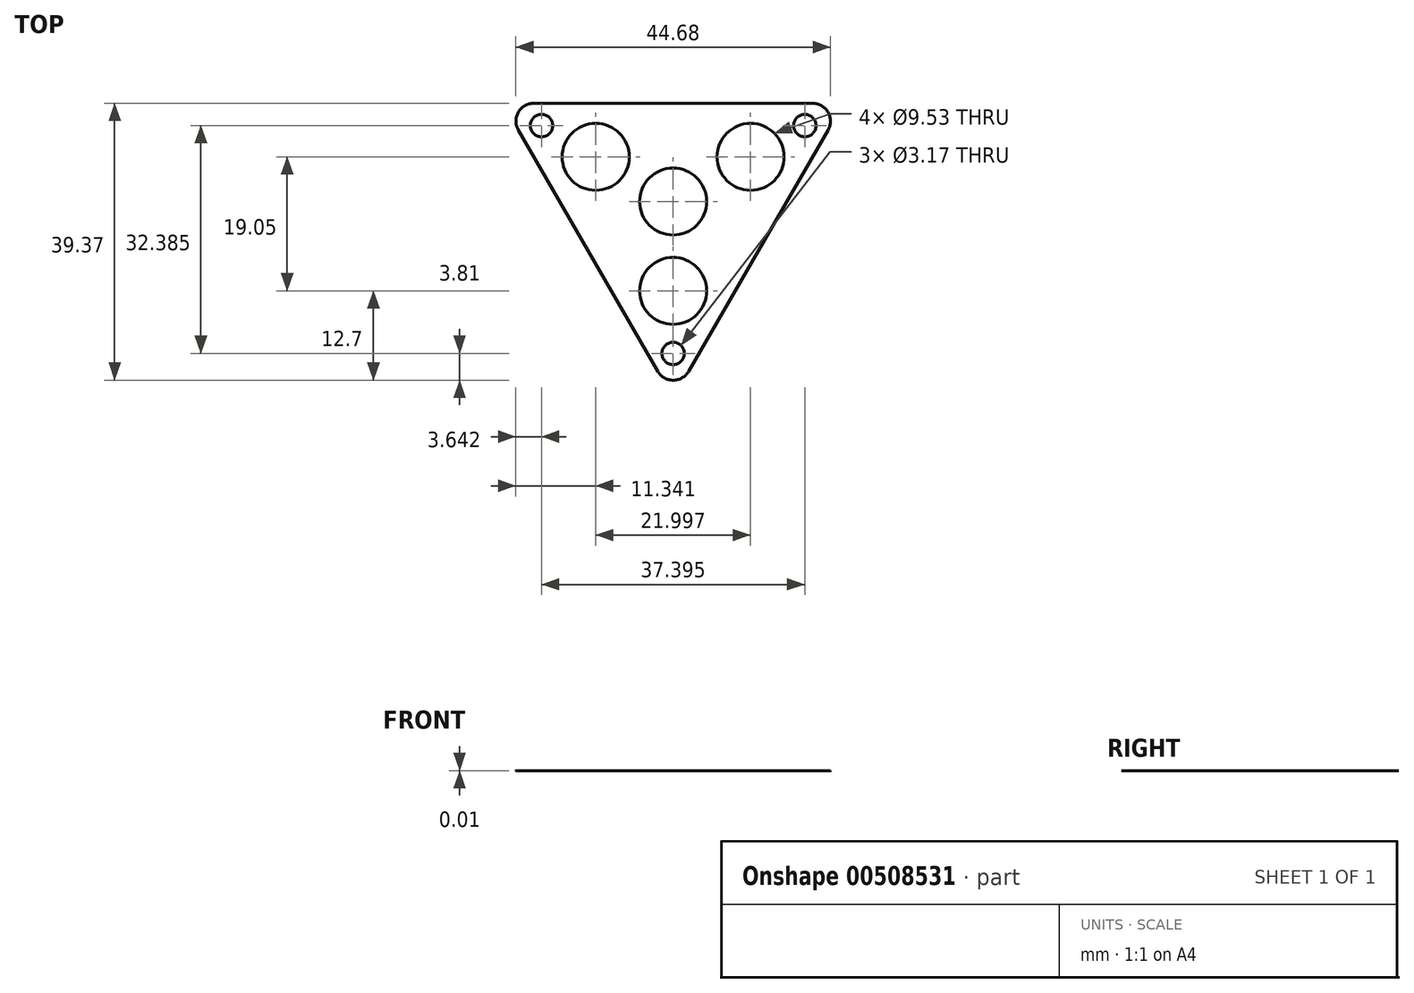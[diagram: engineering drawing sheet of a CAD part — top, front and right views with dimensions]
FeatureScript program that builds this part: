
annotation { "Feature Type Name" : "Feature", "Feature Type Description" : "" }
export const myFeature = defineFeature(function(context is Context, id is Id, definition is map)
    precondition{}
    {
        {
            var Q0;
            Q0=qCreatedBy(makeId("Top.planeOp"),FACE);
            var sketch = newSketch(context, id + "F0", { "sketchPlane" : qUnion([Q0])});
            skCircle(sketch, "E0.cCircle", {"center": v(0, 0) * mm, "radius": 27.94 * mm, "construction": true});
            skLineSegment(sketch, "E0.0", {"start": v(0, -27.94) * mm, "end": v(-24.2, 13.97) * mm});
            skLineSegment(sketch, "E0.1", {"start": v(-24.2, 13.97) * mm, "end": v(24.2, 13.97) * mm});
            skLineSegment(sketch, "E0.2", {"start": v(24.2, 13.97) * mm, "end": v(0, -27.94) * mm});
            skCircle(sketch, "E1.cCircle", {"center": v(0, 0) * mm, "radius": 12.7 * mm, "construction": true});
            skLineSegment(sketch, "E1.0", {"start": v(0, -12.7) * mm, "end": v(-11, 6.35) * mm, "construction": true});
            skLineSegment(sketch, "E1.1", {"start": v(-11, 6.35) * mm, "end": v(11, 6.35) * mm, "construction": true});
            skLineSegment(sketch, "E1.2", {"start": v(11, 6.35) * mm, "end": v(0, -12.7) * mm, "construction": true});
            skCircle(sketch, "E2.cCircle", {"center": v(0, 0) * mm, "radius": 21.59 * mm, "construction": true});
            skLineSegment(sketch, "E2.0", {"start": v(0, -21.59) * mm, "end": v(-18.7, 10.8) * mm, "construction": true});
            skLineSegment(sketch, "E2.1", {"start": v(-18.7, 10.8) * mm, "end": v(18.7, 10.8) * mm, "construction": true});
            skLineSegment(sketch, "E2.2", {"start": v(18.7, 10.8) * mm, "end": v(0, -21.59) * mm, "construction": true});
            skCircle(sketch, "E3", {"center": v(11, 6.35) * mm, "radius": 4.76 * mm});
            skCircle(sketch, "E4", {"center": v(0, -12.7) * mm, "radius": 4.76 * mm});
            skCircle(sketch, "E5", {"center": v(-11, 6.35) * mm, "radius": 4.76 * mm});
            skCircle(sketch, "E6", {"center": v(18.7, 10.8) * mm, "radius": 1.59 * mm});
            skCircle(sketch, "E7", {"center": v(0, -21.59) * mm, "radius": 1.59 * mm});
            skCircle(sketch, "E8", {"center": v(-18.7, 10.8) * mm, "radius": 1.59 * mm});
            skCircle(sketch, "E9", {"center": v(0, 0) * mm, "radius": 4.76 * mm});
            skSolve(sketch);
        }
        {
            var Q0;
            Q0 = qSketchRegion(id + "F0", true);
            extrude(context, id + "F1", {"entities" : qUnion([Q0]), "depth" : 1 / 101.6 * mm});
        }
        {
            var Q0;
            Q0=makeQuery(id+"F1.opExtrude","SWEPT_EDGE",EDGE,{"disambiguationData":[OSD([sQuery(id+"F0.wireOp",EDGE,"E0.0"),sQuery(id+"F0.wireOp",EDGE,"E0.1")])]});
            var Q1;
            Q1=makeQuery(id+"F1.opExtrude","SWEPT_EDGE",EDGE,{"disambiguationData":[OSD([sQuery(id+"F0.wireOp",EDGE,"E0.0"),sQuery(id+"F0.wireOp",EDGE,"E0.2")])]});
            var Q2;
            Q2=makeQuery(id+"F1.opExtrude","SWEPT_EDGE",EDGE,{"disambiguationData":[OSD([sQuery(id+"F0.wireOp",EDGE,"E0.1"),sQuery(id+"F0.wireOp",EDGE,"E0.2")])]});
            fillet(context, id + "F2", {"entities" : qUnion([Q0, Q1, Q2]), "radius" : 2.54 * mm, "tangentPropagation" : true, "allowEdgeOverflow" : false});
        }
    });
